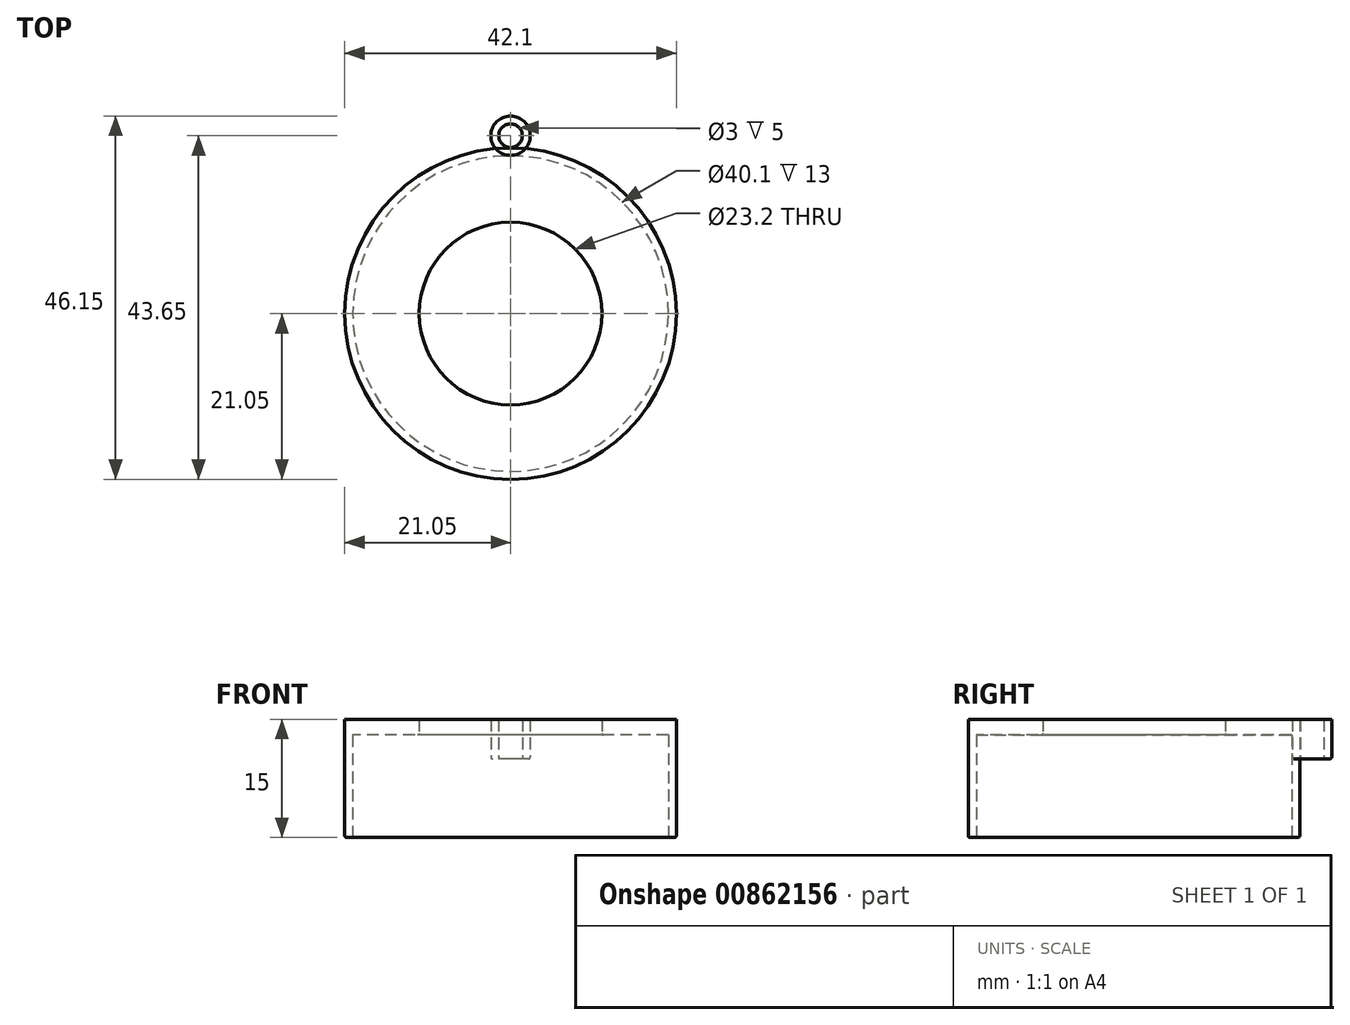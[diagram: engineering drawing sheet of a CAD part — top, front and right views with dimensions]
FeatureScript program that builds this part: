
annotation { "Feature Type Name" : "Feature", "Feature Type Description" : "" }
export const myFeature = defineFeature(function(context is Context, id is Id, definition is map)
    precondition{}
    {
        {
            var Q0;
            Q0=qCreatedBy(makeId("Top.planeOp"),FACE);
            var sketch = newSketch(context, id + "F0", { "sketchPlane" : qUnion([Q0])});
            skCircle(sketch, "E0", {"center": v(0, 0) * mm, "radius": 21.05 * mm});
            skSolve(sketch);
        }
        {
            var Q0;
            Q0 = qSketchRegion(id + "F0", true);
            extrude(context, id + "F1", {"entities" : qUnion([Q0]), "depth" : 15 * mm, "offsetDistance" : 25 * mm});
        }
        {
            var Q0;
            Q0=qCreatedBy(makeId("Top.planeOp"),FACE);
            var sketch = newSketch(context, id + "F2", { "sketchPlane" : qUnion([Q0])});
            skCircle(sketch, "E1", {"center": v(0, 0) * mm, "radius": 20.05 * mm});
            skSolve(sketch);
        }
        {
            var Q0;
            Q0 = qSketchRegion(id + "F2", true);
            extrude(context, id + "F3", {"entities" : qUnion([Q0]), "operationType" : NewBodyOperationType.REMOVE, "depth" : 13 * mm, "offsetDistance" : 25 * mm});
        }
        {
            var Q0;
            Q0=qCreatedBy(makeId("Top.planeOp"),FACE);
            var sketch = newSketch(context, id + "F4", { "sketchPlane" : qUnion([Q0])});
            skCircle(sketch, "E2", {"center": v(0, 0) * mm, "radius": 11.6 * mm});
            skSolve(sketch);
        }
        {
            var Q0;
            Q0 = qSketchRegion(id + "F4", true);
            extrude(context, id + "F5", {"entities" : qUnion([Q0]), "operationType" : NewBodyOperationType.REMOVE, "depth" : 15 * mm, "offsetDistance" : 25 * mm});
        }
        {
            var Q0;
            Q0=qCreatedBy(makeId("Top.planeOp"),FACE);
            var sketch = newSketch(context, id + "F6", { "sketchPlane" : qUnion([Q0])});
            skCircle(sketch, "E3", {"center": v(0, 0) * mm, "radius": 2.5 * mm});
            skSolve(sketch);
        }
        {
            var Q0;
            Q0 = qSketchRegion(id + "F6", true);
            extrude(context, id + "F7", {"entities" : qUnion([Q0]), "depth" : 5 * mm, "offsetDistance" : 25 * mm});
        }
        {
            var Q0;
            Q0=qCreatedBy(makeId("Top.planeOp"),FACE);
            var sketch = newSketch(context, id + "F8", { "sketchPlane" : qUnion([Q0])});
            skCircle(sketch, "E4", {"center": v(0, 0) * mm, "radius": 1.5 * mm});
            skSolve(sketch);
        }
        {
            var Q0;
            Q0 = qSketchRegion(id + "F8", true);
            extrude(context, id + "F9", {"entities" : qUnion([Q0]), "operationType" : NewBodyOperationType.REMOVE, "depth" : 5 * mm, "offsetDistance" : 25 * mm});
        }
        {
            var Q0;
            Q0=makeQuery(id+"F7.opExtrude","SWEPT_BODY",BODY,{"disambiguationData":[OSD([sQuery(id+"F6.wireOp",EDGE,"E3")])]});
            transform(context, id + "F10", {"entities" : qUnion([Q0]), "transformType" : TransformType.TRANSLATION_3D, "dx" : 0 * mm, "dy" : 22.5 * mm, "dz" : 10 * mm, "makeCopy" : false});
        }
        {
            var Q0;
            Q0=makeQuery(id+"F1.opExtrude","CAP_EDGE",EDGE,{"disambiguationData":[OSD([sQuery(id+"F0.wireOp",EDGE,"E0")])],"isStart":true});
            var Q1;
            Q1=makeQuery(id+"F3.boolean.opBoolean","COPY",EDGE,{"derivedFrom":makeQuery(id+"F3.opExtrude","CAP_EDGE",EDGE,{"disambiguationData":[OSD([sQuery(id+"F2.wireOp",EDGE,"E1")])],"isStart":true})});
            var Q2;
            Q2=makeQuery(id+"F5.boolean.opBoolean","INTERSECT",EDGE,{"derivedFrom":[makeQuery(id+"F3.boolean.opBoolean","COPY",FACE,{"derivedFrom":makeQuery(id+"F3.opExtrude","CAP_FACE",FACE,{"disambiguationData":[OSD([sQuery(id+"F2.wireOp",EDGE,"E1")])],"isStart":false})}),makeQuery(id+"F5.opExtrude","SWEPT_FACE",FACE,{"disambiguationData":[OSD([sQuery(id+"F4.wireOp",EDGE,"E2")])]})]});
            var Q3;
            Q3=makeQuery(id+"F9.boolean.opBoolean","COPY",EDGE,{"derivedFrom":makeQuery(id+"F9.opExtrude","CAP_EDGE",EDGE,{"disambiguationData":[OSD([sQuery(id+"F8.wireOp",EDGE,"E4")])],"isStart":true})});
            var Q4;
            Q4=makeQuery(id+"F7.opExtrude","CAP_EDGE",EDGE,{"disambiguationData":[OSD([sQuery(id+"F6.wireOp",EDGE,"E3")])],"isStart":true});
            fillet(context, id + "F11", {"entities" : qUnion([Q0, Q1, Q2, Q3, Q4]), "radius" : 0.2 * mm, "tangentPropagation" : true, "allowEdgeOverflow" : false});
        }
        {
            var Q0;
            Q0=makeQuery(id+"F7.opExtrude","SWEPT_BODY",BODY,{"disambiguationData":[OSD([sQuery(id+"F6.wireOp",EDGE,"E3")])]});
            transform(context, id + "F12", {"entities" : qUnion([Q0]), "transformType" : TransformType.TRANSLATION_3D, "dx" : 0 * mm, "dy" : 0.1 * mm, "dz" : 0 * mm, "makeCopy" : false});
        }
    });
